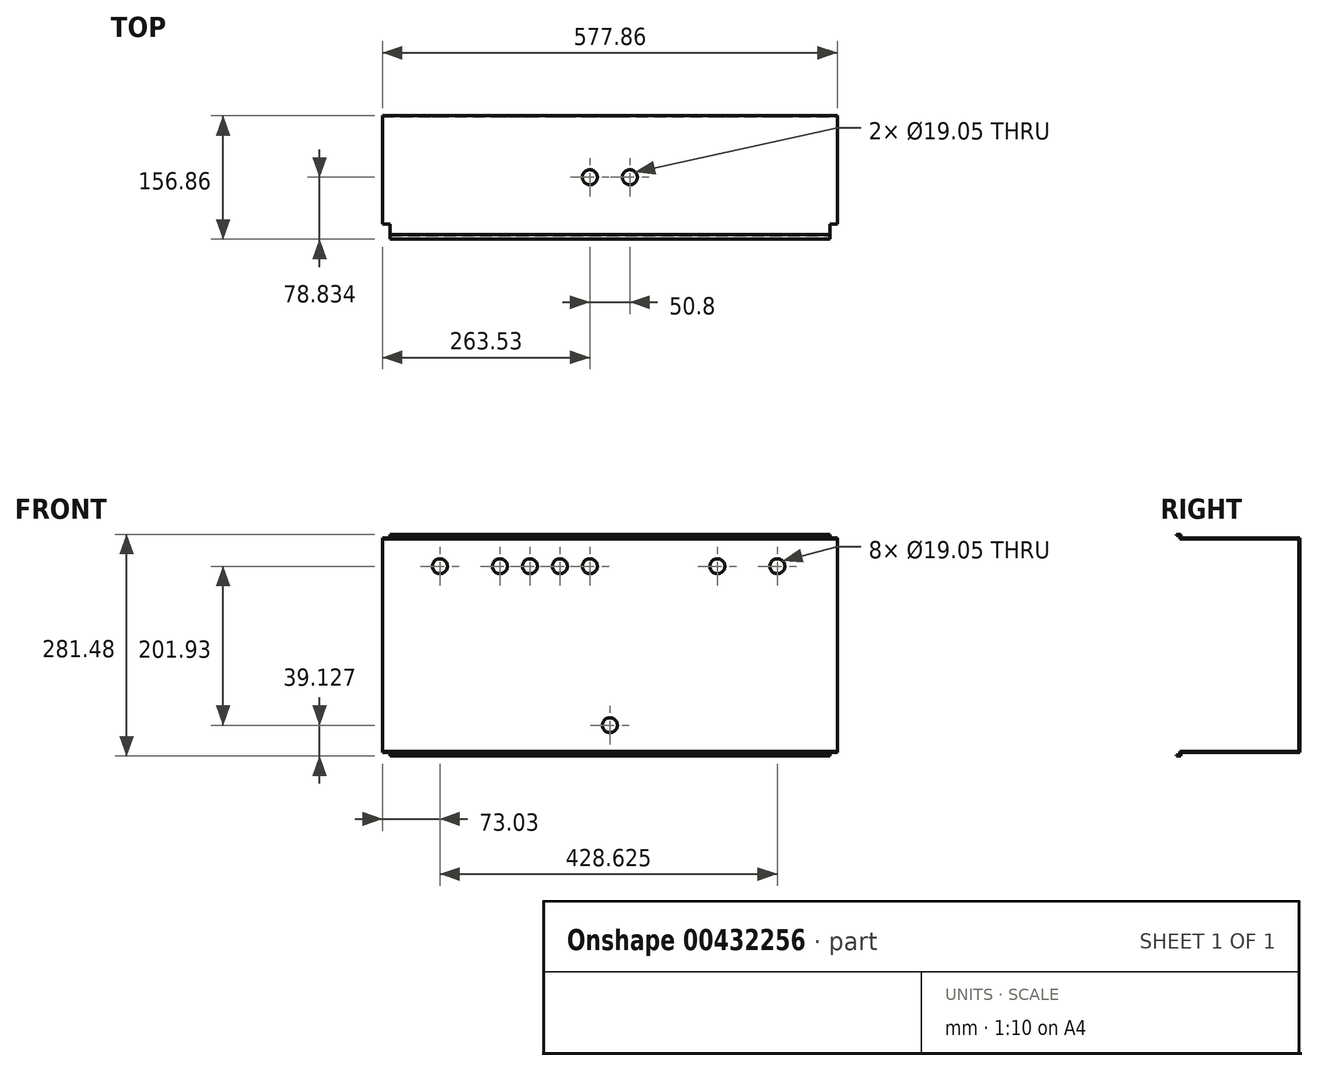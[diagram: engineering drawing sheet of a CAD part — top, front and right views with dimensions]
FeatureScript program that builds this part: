
annotation { "Feature Type Name" : "Feature", "Feature Type Description" : "" }
export const myFeature = defineFeature(function(context is Context, id is Id, definition is map)
    precondition{}
    {
        {
            var Q0;
            Q0=qCreatedBy(makeId("Front.planeOp"),FACE);
            var sketch = newSketch(context, id + "F0", { "sketchPlane" : qUnion([Q0])});
            skLineSegment(sketch, "E0.bottom", {"start": v(-279.4, 287.36) * mm, "end": v(279.4, 287.36) * mm});
            skLineSegment(sketch, "E0.top", {"start": v(-279.4, -287.36) * mm, "end": v(279.4, -287.36) * mm});
            skLineSegment(sketch, "E0.left", {"start": v(-288.93, 264.27) * mm, "end": v(-288.93, -264.27) * mm});
            skLineSegment(sketch, "E0.right", {"start": v(288.93, 264.27) * mm, "end": v(288.93, -264.27) * mm});
            skPoint(sketch, "E0.middle", {"position": v(0, 0) * mm});
            skLineSegment(sketch, "E1.top", {"start": v(-288.93, -264.27) * mm, "end": v(-279.4, -264.27) * mm});
            skLineSegment(sketch, "E1.right", {"start": v(-279.4, -287.36) * mm, "end": v(-279.4, -264.27) * mm});
            skLineSegment(sketch, "E2.top", {"start": v(288.93, -264.27) * mm, "end": v(279.4, -264.27) * mm});
            skLineSegment(sketch, "E2.right", {"start": v(279.4, -287.36) * mm, "end": v(279.4, -264.27) * mm});
            skLineSegment(sketch, "E3.top", {"start": v(288.92, 264.27) * mm, "end": v(279.4, 264.27) * mm});
            skLineSegment(sketch, "E3.right", {"start": v(279.4, 287.36) * mm, "end": v(279.4, 264.27) * mm});
            skLineSegment(sketch, "E4.top", {"start": v(-288.93, 264.27) * mm, "end": v(-279.4, 264.27) * mm});
            skLineSegment(sketch, "E4.right", {"start": v(-279.4, 287.36) * mm, "end": v(-279.4, 264.27) * mm});
            skPoint(sketch, "E4.left.start.orphan", {"position": v(-288.93, 287.36) * mm});
            skPoint(sketch, "E5.orphan", {"position": v(288.93, 287.36) * mm});
            skPoint(sketch, "E6.orphan", {"position": v(288.93, -287.36) * mm});
            skPoint(sketch, "E7.orphan", {"position": v(-288.93, -287.36) * mm});
            skLineSegment(sketch, "E8", {"start": v(0, 333.07) * mm, "end": v(0, -330.5) * mm, "construction": true});
            skLineSegment(sketch, "E9", {"start": v(-371.62, 0) * mm, "end": v(511.85, 0) * mm, "construction": true});
            skCircle(sketch, "E10", {"center": v(0, -101.61) * mm, "radius": 9.53 * mm});
            skCircle(sketch, "E11", {"center": v(-215.9, 100.32) * mm, "radius": 9.53 * mm});
            skCircle(sketch, "E12", {"center": v(-139.7, 100.32) * mm, "radius": 9.53 * mm});
            skCircle(sketch, "E13", {"center": v(-101.6, 100.32) * mm, "radius": 9.53 * mm});
            skCircle(sketch, "E14", {"center": v(-63.5, 100.32) * mm, "radius": 9.53 * mm});
            skCircle(sketch, "E15", {"center": v(-25.4, 100.32) * mm, "radius": 9.53 * mm});
            skCircle(sketch, "E16", {"center": v(136.53, 100.32) * mm, "radius": 9.53 * mm});
            skCircle(sketch, "E17", {"center": v(212.72, 100.32) * mm, "radius": 9.53 * mm});
            skSolve(sketch);
        }
        {
            var Q0;
            Q0 = qSketchRegion(id + "F0", true);
            extrude(context, id + "F1", {"entities" : qUnion([Q0]), "depth" : 1.27 * mm, "offsetDistance" : 25.4 * mm});
        }
        {
            var Q0;
            Q0=makeQuery(id+"F1.opExtrude","CAP_FACE",FACE,{"disambiguationData":[OSD([sQuery(id+"F0.wireOp",EDGE,"E0.bottom"),sQuery(id+"F0.wireOp",EDGE,"E0.top"),sQuery(id+"F0.wireOp",EDGE,"E0.left"),sQuery(id+"F0.wireOp",EDGE,"E0.right"),sQuery(id+"F0.wireOp",EDGE,"E1.top"),sQuery(id+"F0.wireOp",EDGE,"E1.right"),sQuery(id+"F0.wireOp",EDGE,"E2.top"),sQuery(id+"F0.wireOp",EDGE,"E2.right"),sQuery(id+"F0.wireOp",EDGE,"E3.top"),sQuery(id+"F0.wireOp",EDGE,"E3.right"),sQuery(id+"F0.wireOp",EDGE,"E4.top"),sQuery(id+"F0.wireOp",EDGE,"E4.right"),sQuery(id+"F0.wireOp",EDGE,"E10"),sQuery(id+"F0.wireOp",EDGE,"E11"),sQuery(id+"F0.wireOp",EDGE,"E12"),sQuery(id+"F0.wireOp",EDGE,"E13"),sQuery(id+"F0.wireOp",EDGE,"E14"),sQuery(id+"F0.wireOp",EDGE,"E15"),sQuery(id+"F0.wireOp",EDGE,"E16"),sQuery(id+"F0.wireOp",EDGE,"E17")])],"isStart":false});
            var sketch = newSketch(context, id + "F2", { "sketchPlane" : qUnion([Q0])});
            skLineSegment(sketch, "E18", {"start": v(-288.93, 134.7) * mm, "end": v(288.93, 134.7) * mm});
            skLineSegment(sketch, "E19", {"start": v(-288.93, -134.7) * mm, "end": v(288.93, -134.7) * mm});
            skLineSegment(sketch, "E20", {"start": v(-279.4, 282.6) * mm, "end": v(279.4, 282.6) * mm});
            skLineSegment(sketch, "E21", {"start": v(-279.4, 273.08) * mm, "end": v(279.4, 273.08) * mm});
            skLineSegment(sketch, "E22", {"start": v(279.4, 277.84) * mm, "end": v(-279.4, 277.84) * mm});
            skLineSegment(sketch, "E23.MirrorCS", {"start": v(-279.4, -282.6) * mm, "end": v(279.4, -282.6) * mm});
            skLineSegment(sketch, "E24.MirrorCS", {"start": v(-279.4, -273.08) * mm, "end": v(279.4, -273.08) * mm});
            skLineSegment(sketch, "E25.MirrorCS", {"start": v(279.4, -277.84) * mm, "end": v(-279.4, -277.84) * mm});
            skLineSegment(sketch, "E26.bottom", {"start": v(288.93, 134.7) * mm, "end": v(-288.93, 134.7) * mm});
            skLineSegment(sketch, "E26.top", {"start": v(288.93, 135.98) * mm, "end": v(-288.93, 135.98) * mm});
            skLineSegment(sketch, "E26.left", {"start": v(288.93, 134.7) * mm, "end": v(288.93, 135.98) * mm});
            skLineSegment(sketch, "E26.right", {"start": v(-288.93, 134.7) * mm, "end": v(-288.93, 135.98) * mm});
            skLineSegment(sketch, "E27.bottom", {"start": v(288.93, -134.7) * mm, "end": v(-288.93, -134.7) * mm});
            skLineSegment(sketch, "E27.top", {"start": v(288.93, -135.98) * mm, "end": v(-288.93, -135.98) * mm});
            skLineSegment(sketch, "E27.left", {"start": v(288.93, -134.7) * mm, "end": v(288.93, -135.98) * mm});
            skLineSegment(sketch, "E27.right", {"start": v(-288.93, -134.7) * mm, "end": v(-288.93, -135.98) * mm});
            skSolve(sketch);
        }
        {
            var Q0;
            Q0 = qSketchRegion(id + "F2", true);
            extrude(context, id + "F3", {"entities" : qUnion([Q0]), "operationType" : NewBodyOperationType.ADD, "depth" : 150.83 * mm, "offsetDistance" : 25.4 * mm});
        }
        {
            var Q0;
            Q0=makeQuery(id+"F3.opExtrude","SWEPT_FACE",FACE,{"disambiguationData":[OSD([sQuery(id+"F2.wireOp",EDGE,"E27.top")])]});
            var sketch = newSketch(context, id + "F4", { "sketchPlane" : qUnion([Q0])});
            skLineSegment(sketch, "E28.bottom", {"start": v(-288.93, 152.1) * mm, "end": v(288.93, 152.1) * mm});
            skLineSegment(sketch, "E28.top", {"start": v(-288.93, 150.83) * mm, "end": v(288.93, 150.83) * mm});
            skLineSegment(sketch, "E28.left", {"start": v(-288.93, 152.1) * mm, "end": v(-288.93, 150.83) * mm});
            skLineSegment(sketch, "E28.right", {"start": v(288.93, 152.1) * mm, "end": v(288.93, 150.83) * mm});
            skSolve(sketch);
        }
        {
            var Q0;
            Q0 = qSketchRegion(id + "F4", true);
            extrude(context, id + "F5", {"entities" : qUnion([Q0]), "operationType" : NewBodyOperationType.ADD, "depth" : 4.76 * mm, "offsetDistance" : 25.4 * mm});
        }
        {
            var Q0;
            Q0=makeQuery(id+"F5.boolean.opBoolean","MERGE",FACE,{"derivedFrom":[makeQuery(id+"F3.opExtrude","CAP_FACE",FACE,{"disambiguationData":[OSD([sQuery(id+"F2.wireOp",EDGE,"E27.bottom"),sQuery(id+"F2.wireOp",EDGE,"E27.top"),sQuery(id+"F2.wireOp",EDGE,"E27.left"),sQuery(id+"F2.wireOp",EDGE,"E27.right")])],"isStart":false}),makeQuery(id+"F5.opExtrude","SWEPT_FACE",FACE,{"disambiguationData":[OSD([sQuery(id+"F4.wireOp",EDGE,"E28.bottom")])]})]});
            var sketch = newSketch(context, id + "F6", { "sketchPlane" : qUnion([Q0])});
            skLineSegment(sketch, "E29.bottom", {"start": v(288.93, -140.74) * mm, "end": v(-288.93, -140.74) * mm});
            skLineSegment(sketch, "E29.top", {"start": v(288.93, -139.47) * mm, "end": v(-288.93, -139.47) * mm});
            skLineSegment(sketch, "E29.left", {"start": v(288.93, -140.74) * mm, "end": v(288.93, -139.47) * mm});
            skLineSegment(sketch, "E29.right", {"start": v(-288.93, -140.74) * mm, "end": v(-288.93, -139.47) * mm});
            skSolve(sketch);
        }
        {
            var Q0;
            Q0 = qSketchRegion(id + "F6", true);
            extrude(context, id + "F7", {"entities" : qUnion([Q0]), "operationType" : NewBodyOperationType.ADD, "depth" : 4.76 * mm, "offsetDistance" : 25.4 * mm});
        }
        {
            var Q0;
            Q0=makeQuery(id+"F7.boolean.opBoolean","MERGE",FACE,{"derivedFrom":[makeQuery(id+"F5.boolean.opBoolean","MERGE",FACE,{"derivedFrom":[makeQuery(id+"F3.boolean.opBoolean","MERGE",FACE,{"derivedFrom":[makeQuery(id+"F1.opExtrude","SWEPT_FACE",FACE,{"disambiguationData":[OSD([sQuery(id+"F0.wireOp",EDGE,"E0.left")])]}),makeQuery(id+"F3.opExtrude","SWEPT_FACE",FACE,{"disambiguationData":[OSD([sQuery(id+"F2.wireOp",EDGE,"E26.right")])]}),makeQuery(id+"F3.opExtrude","SWEPT_FACE",FACE,{"disambiguationData":[OSD([sQuery(id+"F2.wireOp",EDGE,"E27.right")])]})]}),makeQuery(id+"F5.opExtrude","SWEPT_FACE",FACE,{"disambiguationData":[OSD([sQuery(id+"F4.wireOp",EDGE,"E28.left")])]})]}),makeQuery(id+"F7.opExtrude","SWEPT_FACE",FACE,{"disambiguationData":[OSD([sQuery(id+"F6.wireOp",EDGE,"E29.right")])]})]});
            var sketch = newSketch(context, id + "F8", { "sketchPlane" : qUnion([Q0])});
            skLineSegment(sketch, "E30", {"start": v(150.83, 135.98) * mm, "end": v(150.83, 140.74) * mm});
            skLineSegment(sketch, "E31", {"start": v(150.83, 140.74) * mm, "end": v(156.84, 140.74) * mm});
            skLineSegment(sketch, "E32", {"start": v(156.84, 140.74) * mm, "end": v(156.84, 139.47) * mm});
            skLineSegment(sketch, "E33", {"start": v(156.84, 139.47) * mm, "end": v(152.1, 139.47) * mm});
            skLineSegment(sketch, "E34", {"start": v(152.1, 139.47) * mm, "end": v(152.1, 135.98) * mm});
            skLineSegment(sketch, "E35", {"start": v(150.83, 135.98) * mm, "end": v(152.1, 135.98) * mm});
            skSolve(sketch);
        }
        {
            var Q0;
            Q0=makeQuery(id+"F8.imprint","IMPRINT",FACE,{"disambiguationData":[TD([[makeQuery(id+"F8.imprint","IMPRINT",EDGE,{"derivedFrom":sQuery(id+"F8.wireOp",EDGE,"E30")}),-1.0]])]});
            var Q1;
            Q1=sQuery(id+"F8.wireOp",EDGE,"E32");
            var Q2;
            Q2=sQuery(id+"F8.wireOp",EDGE,"E33");
            var Q3;
            Q3=sQuery(id+"F8.wireOp",EDGE,"E31");
            var Q4;
            Q4=sQuery(id+"F8.wireOp",EDGE,"E30");
            var Q5;
            Q5=sQuery(id+"F8.wireOp",EDGE,"E34");
            var Q6;
            Q6=sQuery(id+"F8.wireOp",EDGE,"E35");
            extrude(context, id + "F9", {"entities" : qUnion([Q0]), "operationType" : NewBodyOperationType.ADD, "surfaceOperationType" : NewSurfaceOperationType.ADD, "surfaceEntities" : qUnion([Q1, Q2, Q3, Q4, Q5, Q6]), "oppositeDirection" : true, "depth" : 577.85 * mm, "offsetDistance" : 25.4 * mm});
        }
        {
            var Q0;
            {var subQ0=sQuery(id+"F0.wireOp",EDGE,"E2.right");var subQ1=sQuery(id+"F0.wireOp",EDGE,"E2.top");var subQ2=sQuery(id+"F0.wireOp",EDGE,"E1.right");var subQ3=sQuery(id+"F0.wireOp",EDGE,"E0.top");var subQ4=sQuery(id+"F0.wireOp",EDGE,"E0.left");var subQ5=sQuery(id+"F0.wireOp",EDGE,"E0.right");var subQ6=sQuery(id+"F0.wireOp",EDGE,"E1.top");Q0=makeQuery(id+"F3.boolean.opBoolean","SPLIT",FACE,{"disambiguationData":[TD([makeQuery(id+"F1.opExtrude","SWEPT_FACE",FACE,{"disambiguationData":[OSD([subQ3])]})])],"derivedFrom":makeQuery(id+"F1.opExtrude","CAP_FACE",FACE,{"disambiguationData":[OSD([sQuery(id+"F0.wireOp",EDGE,"E0.bottom"),subQ3,subQ4,subQ5,subQ6,subQ2,subQ1,subQ0,sQuery(id+"F0.wireOp",EDGE,"E3.top"),sQuery(id+"F0.wireOp",EDGE,"E3.right"),sQuery(id+"F0.wireOp",EDGE,"E4.top"),sQuery(id+"F0.wireOp",EDGE,"E4.right"),sQuery(id+"F0.wireOp",EDGE,"E10"),sQuery(id+"F0.wireOp",EDGE,"E11"),sQuery(id+"F0.wireOp",EDGE,"E12"),sQuery(id+"F0.wireOp",EDGE,"E13"),sQuery(id+"F0.wireOp",EDGE,"E14"),sQuery(id+"F0.wireOp",EDGE,"E15"),sQuery(id+"F0.wireOp",EDGE,"E16"),sQuery(id+"F0.wireOp",EDGE,"E17")])],"isStart":false})});}
            var Q1;
            {var subQ0=sQuery(id+"F0.wireOp",EDGE,"E4.right");var subQ1=sQuery(id+"F0.wireOp",EDGE,"E4.top");var subQ2=sQuery(id+"F0.wireOp",EDGE,"E3.right");var subQ3=sQuery(id+"F0.wireOp",EDGE,"E0.bottom");var subQ4=sQuery(id+"F0.wireOp",EDGE,"E0.right");var subQ5=sQuery(id+"F0.wireOp",EDGE,"E3.top");var subQ6=sQuery(id+"F0.wireOp",EDGE,"E0.left");Q1=makeQuery(id+"F3.boolean.opBoolean","SPLIT",FACE,{"disambiguationData":[TD([makeQuery(id+"F1.opExtrude","SWEPT_FACE",FACE,{"disambiguationData":[OSD([subQ3])]})])],"derivedFrom":makeQuery(id+"F1.opExtrude","CAP_FACE",FACE,{"disambiguationData":[OSD([subQ3,sQuery(id+"F0.wireOp",EDGE,"E0.top"),subQ6,subQ4,sQuery(id+"F0.wireOp",EDGE,"E1.top"),sQuery(id+"F0.wireOp",EDGE,"E1.right"),sQuery(id+"F0.wireOp",EDGE,"E2.top"),sQuery(id+"F0.wireOp",EDGE,"E2.right"),subQ5,subQ2,subQ1,subQ0,sQuery(id+"F0.wireOp",EDGE,"E10"),sQuery(id+"F0.wireOp",EDGE,"E11"),sQuery(id+"F0.wireOp",EDGE,"E12"),sQuery(id+"F0.wireOp",EDGE,"E13"),sQuery(id+"F0.wireOp",EDGE,"E14"),sQuery(id+"F0.wireOp",EDGE,"E15"),sQuery(id+"F0.wireOp",EDGE,"E16"),sQuery(id+"F0.wireOp",EDGE,"E17")])],"isStart":false})});}
            extrude(context, id + "F10", {"entities" : qUnion([Q0, Q1]), "operationType" : NewBodyOperationType.REMOVE, "oppositeDirection" : true, "depth" : 25.4 * mm, "offsetDistance" : 25.4 * mm});
        }
        {
            var Q0;
            {var subQ0=sQuery(id+"F2.wireOp",EDGE,"E26.top");Q0=makeQuery(id+"F10.boolean.opBoolean","MERGE",FACE,{"derivedFrom":[makeQuery(id+"F3.opExtrude","SWEPT_FACE",FACE,{"disambiguationData":[OSD([subQ0])]}),makeQuery(id+"F10.opExtrude","SWEPT_FACE",FACE,{"disambiguationData":[OSD([subQ0])]})]});}
            var sketch = newSketch(context, id + "F11", { "sketchPlane" : qUnion([Q0])});
            skCircle(sketch, "E36", {"center": v(25.4, -78.03) * mm, "radius": 9.53 * mm});
            skCircle(sketch, "E37", {"center": v(-25.4, -78.03) * mm, "radius": 9.53 * mm});
            skSolve(sketch);
        }
        {
            var Q0;
            Q0 = qSketchRegion(id + "F11", true);
            extrude(context, id + "F12", {"entities" : qUnion([Q0]), "operationType" : NewBodyOperationType.REMOVE, "oppositeDirection" : true, "depth" : 25.4 * mm, "offsetDistance" : 25.4 * mm});
        }
        {
            var Q0;
            Q0=makeQuery(id+"F9.opExtrude","SWEPT_FACE",FACE,{"disambiguationData":[OSD([sQuery(id+"F8.wireOp",EDGE,"E31")])]});
            var sketch = newSketch(context, id + "F13", { "sketchPlane" : qUnion([Q0])});
            skLineSegment(sketch, "E38.bottom", {"start": v(-288.93, -156.84) * mm, "end": v(-279.4, -156.84) * mm});
            skLineSegment(sketch, "E38.top", {"start": v(-288.93, -137.8) * mm, "end": v(-279.4, -137.8) * mm});
            skLineSegment(sketch, "E38.left", {"start": v(-288.93, -156.84) * mm, "end": v(-288.93, -137.8) * mm});
            skLineSegment(sketch, "E38.right", {"start": v(-279.4, -156.84) * mm, "end": v(-279.4, -137.8) * mm});
            skLineSegment(sketch, "E39.bottom", {"start": v(288.93, -156.84) * mm, "end": v(279.4, -156.84) * mm});
            skLineSegment(sketch, "E39.top", {"start": v(288.93, -137.8) * mm, "end": v(279.4, -137.8) * mm});
            skLineSegment(sketch, "E39.left", {"start": v(288.93, -156.84) * mm, "end": v(288.93, -137.8) * mm});
            skLineSegment(sketch, "E39.right", {"start": v(279.4, -156.84) * mm, "end": v(279.4, -137.8) * mm});
            skLineSegment(sketch, "E40.bottom", {"start": v(279.4, -156.84) * mm, "end": v(292.23, -156.84) * mm});
            skLineSegment(sketch, "E40.top", {"start": v(279.4, -157.68) * mm, "end": v(292.23, -157.68) * mm});
            skLineSegment(sketch, "E40.left", {"start": v(279.4, -156.84) * mm, "end": v(279.4, -157.68) * mm});
            skLineSegment(sketch, "E40.right", {"start": v(292.23, -156.84) * mm, "end": v(292.23, -157.68) * mm});
            skLineSegment(sketch, "E41.bottom", {"start": v(-279.4, -156.84) * mm, "end": v(-289.98, -156.84) * mm});
            skLineSegment(sketch, "E41.top", {"start": v(-279.4, -157.68) * mm, "end": v(-289.98, -157.68) * mm});
            skLineSegment(sketch, "E41.left", {"start": v(-279.4, -156.84) * mm, "end": v(-279.4, -157.68) * mm});
            skLineSegment(sketch, "E41.right", {"start": v(-289.98, -156.84) * mm, "end": v(-289.98, -157.68) * mm});
            skSolve(sketch);
        }
        {
            var Q0;
            Q0 = qSketchRegion(id + "F13", true);
            extrude(context, id + "F14", {"entities" : qUnion([Q0]), "operationType" : NewBodyOperationType.REMOVE, "endBound" : BoundingType.THROUGH_ALL, "oppositeDirection" : true, "depth" : 25.4 * mm, "offsetDistance" : 25.4 * mm});
        }
    });
